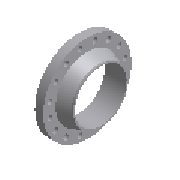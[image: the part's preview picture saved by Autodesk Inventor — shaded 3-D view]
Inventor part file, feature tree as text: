
AUTODESK INVENTOR PART (.ipt)
format: ipt  version: 2017.3 (Build 213257000, 257)  size: 279,040 bytes
history: native  units: mm (DEFAULTED — no unit token found)
features: other x4, sketch x3, revolve x2, chamfer x2, extrude x1, pattern_circular x1, fillet x1
ambient origin geometry x8: Origin, YZ Plane, XZ Plane, XY Plane, X Axis, Y Axis, Z Axis, Center Point
bodies: Body1 (feature_tree)
feature tree (14):
  revolve  "Revolution1"  [1 undecoded]
  extrude  "Extrusion1"  Depth=1.524mm
  pattern_circular  "Circular Pattern1"  [2 undecoded]
  other  "Work Axis1"
  other  "Work Point1"
  other  "Work Axis2"
  other  "Work Point2"
  chamfer  "Chamfer1"  Angle=90.0deg  [1 undecoded]
  revolve  "Revolution2"  [1 undecoded]
  fillet  "Fillet1"  Radius=31.75mm
  chamfer  "Chamfer2"  Distance=25.4mm
  sketch  "Sketch1"  dims[d0=520.7mm d1=381.0mm]
  sketch  "Sketch2"  dims[d2=1.524mm d3=320.675mm]
  sketch  "Sketch3"  dims[d4=323.85mm d7=374.65mm d9=90.0deg d10=225.425mm d11=31.75mm d12=25.4mm d13=0.0mm d14=160.0mm d16=360.0deg d17=1.963495mm d18=49.276mm d20=128.524mm d21=14.280444mm d22=1.5875mm d23=3.175mm d24=45.0deg d25=25.4mm d26=330.2mm d27=355.6mm d28=1.5875mm d29=6.544985mm d30=12.7mm d31=82.55mm d32=11.1125mm d33=2.585579mm d34=90.0deg d35=0.79375mm d36=0.79375mm d37=3.175mm d38=45.0deg]
note: 5 required parameter values undecoded (feature->parameter linkage not recoverable at this tier; creation-order binding heuristic only, values carry confidence <= 0.55)